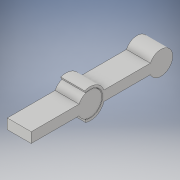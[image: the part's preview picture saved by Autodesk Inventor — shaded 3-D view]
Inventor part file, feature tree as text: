
AUTODESK INVENTOR PART (.ipt)
format: ipt  version: 2018 (Build 220112000, 112)  size: 117,760 bytes
history: native  units: in
note: dims shown in document units (in); Inventor stores cm internally (conversion verified against a paired STEP export)
features: extrude x1, sketch x1
ambient origin geometry x8: Origin, YZ Plane, XZ Plane, XY Plane, X Axis, Y Axis, Z Axis, Center Point
bodies: Body1 (feature_tree)
feature tree (2):
  extrude  "Extrusion2"  Depth=0.25in
  sketch  "Sketch1"  dims[d0=0.25in d4=0.5in d12=0.025in d13=0.025in d15=0.25in d16=0.0in]
